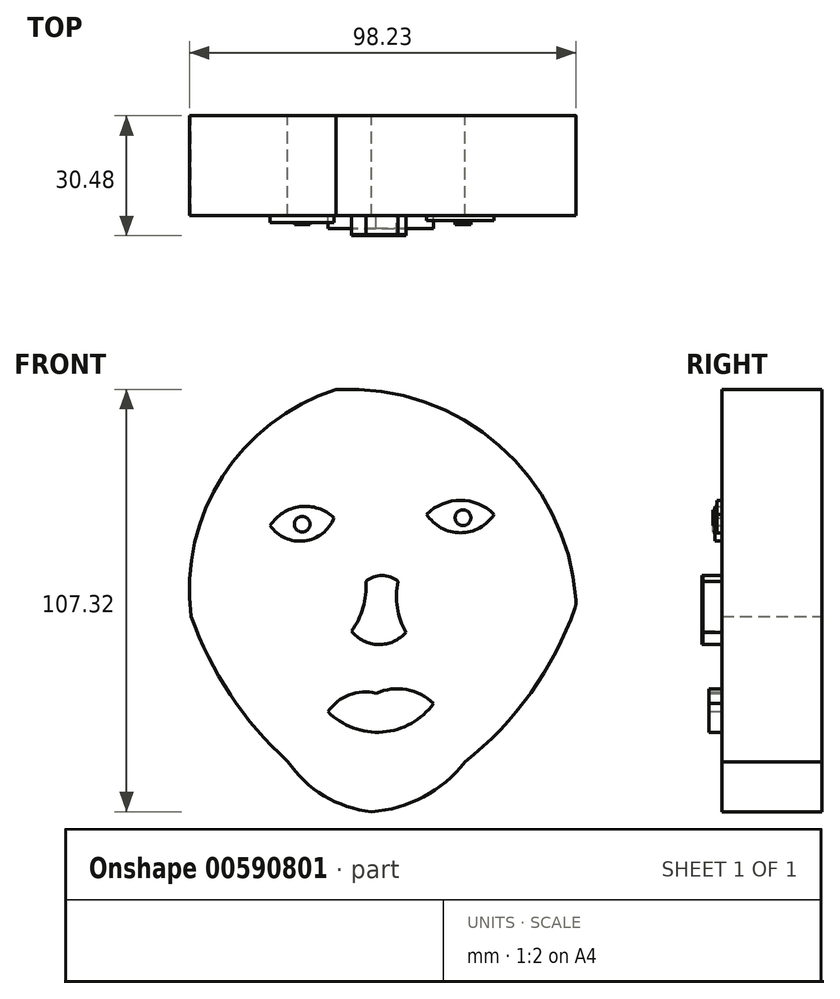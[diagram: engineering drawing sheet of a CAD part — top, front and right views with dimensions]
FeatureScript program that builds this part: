
annotation { "Feature Type Name" : "Feature", "Feature Type Description" : "" }
export const myFeature = defineFeature(function(context is Context, id is Id, definition is map)
    precondition{}
    {
        {
            var Q0;
            Q0=qCreatedBy(makeId("Front.planeOp"),FACE);
            var sketch = newSketch(context, id + "F0", { "sketchPlane" : qUnion([Q0])});
            skArc(sketch, "E0", {"start": v(-3.94, 54.48) * mm, "mid": v(-32.78, 32.37) * mm, "end": v(-40.74, -3.09) * mm});
            skArc(sketch, "E1", {"start": v(57.11, 0) * mm, "mid": v(37.92, 39.94) * mm, "end": v(-3.94, 54.48) * mm});
            skArc(sketch, "E2", {"start": v(-40.74, -3.09) * mm, "mid": v(-30.78, -23.03) * mm, "end": v(-16.23, -39.9) * mm});
            skArc(sketch, "E3", {"start": v(-16.23, -39.9) * mm, "mid": v(-7, -48.7) * mm, "end": v(5.1, -52.74) * mm});
            skArc(sketch, "E4", {"start": v(5.1, -52.74) * mm, "mid": v(18.29, -48.98) * mm, "end": v(28.77, -40.15) * mm});
            skArc(sketch, "E5", {"start": v(28.77, -40.15) * mm, "mid": v(45.86, -22.13) * mm, "end": v(57.11, 0) * mm});
            skSolve(sketch);
        }
        {
            var Q0;
            Q0=makeQuery(id+"F0.imprint","IMPRINT",FACE,{"disambiguationData":[TD([[makeQuery(id+"F0.imprint","IMPRINT",EDGE,{"derivedFrom":sQuery(id+"F0.wireOp",EDGE,"E0")}),1.0]])]});
            extrude(context, id + "F1", {"entities" : qUnion([Q0]), "depth" : 25.4 * mm, "offsetDistance" : 25.4 * mm});
        }
        {
            var Q0;
            Q0=makeQuery(id+"F1.opExtrude","SWEPT_EDGE",EDGE,{"disambiguationData":[OSD([sQuery(id+"F0.wireOp",EDGE,"E1"),sQuery(id+"F0.wireOp",EDGE,"E5")])]});
            fillet(context, id + "F2", {"entities" : qUnion([Q0]), "radius" : 5.08 * mm, "tangentPropagation" : true, "allowEdgeOverflow" : false});
        }
        {
            var Q0;
            Q0=makeQuery(id+"F1.opExtrude","CAP_FACE",FACE,{"disambiguationData":[OSD([sQuery(id+"F0.wireOp",EDGE,"E0"),sQuery(id+"F0.wireOp",EDGE,"E1"),sQuery(id+"F0.wireOp",EDGE,"E2"),sQuery(id+"F0.wireOp",EDGE,"E3"),sQuery(id+"F0.wireOp",EDGE,"E4"),sQuery(id+"F0.wireOp",EDGE,"E5")])],"isStart":false});
            var sketch = newSketch(context, id + "F3", { "sketchPlane" : qUnion([Q0])});
            skArc(sketch, "E6", {"start": v(-11.83, 44.82) * mm, "mid": v(-25.26, 50.26) * mm, "end": v(-38.7, 44.82) * mm});
            skArc(sketch, "E7", {"start": v(-29.05, 57.96) * mm, "mid": v(-21.73, 49.7) * mm, "end": v(-11.83, 44.82) * mm});
            skArc(sketch, "E8", {"start": v(-8.03, 62.64) * mm, "mid": v(-11.09, 53.98) * mm, "end": v(-11.83, 44.82) * mm});
            skArc(sketch, "E9", {"start": v(-18.25, 60) * mm, "mid": v(-14.37, 51.2) * mm, "end": v(-7.15, 44.82) * mm});
            skSolve(sketch);
        }
        {
            var Q0;
            {var subQ9=sQuery(id+"F0.wireOp",EDGE,"E2");var subQ14=makeQuery(id+"F1.opExtrude","CAP_EDGE",EDGE,{"disambiguationData":[OSD([subQ9])],"isStart":false});Q0=makeQuery(id+"F3.imprint","IMPRINT",FACE,{"disambiguationData":[TD([[makeQuery(id+"F3.imprint","IMPRINT",EDGE,{"derivedFrom":subQ14}),1.0]])]});}
            var sketch = newSketch(context, id + "F4", { "sketchPlane" : qUnion([Q0])});
            skArc(sketch, "E10", {"start": v(-9.29, 45.39) * mm, "mid": v(-22.19, 52.37) * mm, "end": v(-36.77, 50.8) * mm});
            skArc(sketch, "E11", {"start": v(2.4, 50.3) * mm, "mid": v(-9.6, 54.9) * mm, "end": v(-22.19, 57.5) * mm});
            skPoint(sketch, "E11.endSnap0", {"position": v(-22.19, 52.37) * mm});
            skArc(sketch, "E12", {"start": v(2.4, 50.3) * mm, "mid": v(-8.36, 51.52) * mm, "end": v(-19.18, 51.58) * mm});
            skArc(sketch, "E13", {"start": v(36.1, 50.3) * mm, "mid": v(22.77, 53.24) * mm, "end": v(9.43, 50.3) * mm});
            skArc(sketch, "E14", {"start": v(36.1, 50.3) * mm, "mid": v(26.93, 50.7) * mm, "end": v(19.45, 45.39) * mm});
            skArc(sketch, "E15", {"start": v(45.24, 45.39) * mm, "mid": v(37.3, 45.56) * mm, "end": v(30.92, 40.8) * mm});
            skArc(sketch, "E16", {"start": v(42.8, 50.3) * mm, "mid": v(33.75, 49.76) * mm, "end": v(25.81, 45.39) * mm});
            skArc(sketch, "E17", {"start": v(42.8, 50.3) * mm, "mid": v(36.17, 49.52) * mm, "end": v(30.92, 45.39) * mm});
            skArc(sketch, "E18", {"start": v(38.66, 53.24) * mm, "mid": v(26.57, 57.77) * mm, "end": v(16.03, 50.3) * mm});
            skPoint(sketch, "E18.startSnap0", {"position": v(22.77, 53.24) * mm});
            skArc(sketch, "E19", {"start": v(58.53, 45.39) * mm, "mid": v(46.41, 44.63) * mm, "end": v(36.1, 38.2) * mm});
            skArc(sketch, "E20", {"start": v(51.08, 53.24) * mm, "mid": v(41.2, 49.1) * mm, "end": v(32.58, 42.76) * mm});
            skArc(sketch, "E21", {"start": v(29.89, 55.18) * mm, "mid": v(19.27, 57.62) * mm, "end": v(9.43, 52.97) * mm});
            skArc(sketch, "E22", {"start": v(2.4, 52.97) * mm, "mid": v(-9.37, 58.06) * mm, "end": v(-22.19, 57.5) * mm});
            skArc(sketch, "E23", {"start": v(-13.81, 42.73) * mm, "mid": v(-24, 47.77) * mm, "end": v(-34.79, 44.23) * mm});
            skArc(sketch, "E24", {"start": v(-14.54, 40.13) * mm, "mid": v(-22.74, 43.62) * mm, "end": v(-31.61, 42.73) * mm});
            skArc(sketch, "E25", {"start": v(-4.54, 46.3) * mm, "mid": v(-12.16, 52.84) * mm, "end": v(-22.19, 52.97) * mm});
            skArc(sketch, "E26", {"start": v(29.89, 55.18) * mm, "mid": v(16.98, 58.22) * mm, "end": v(4.8, 52.97) * mm});
            skArc(sketch, "E27", {"start": v(47.63, 48) * mm, "mid": v(34.16, 46.75) * mm, "end": v(24.61, 37.16) * mm});
            skArc(sketch, "E28", {"start": v(53.1, 40.8) * mm, "mid": v(43.8, 39.51) * mm, "end": v(36.1, 34.08) * mm});
            skArc(sketch, "E29", {"start": v(0, 46.3) * mm, "mid": v(-6.13, 51) * mm, "end": v(-13.81, 50.3) * mm});
            skArc(sketch, "E30", {"start": v(0, 40.8) * mm, "mid": v(-6.55, 48.04) * mm, "end": v(-16.04, 50.3) * mm});
            skArc(sketch, "E31", {"start": v(29.89, 55.18) * mm, "mid": v(18.87, 51.99) * mm, "end": v(9.5, 45.39) * mm});
            skArc(sketch, "E32", {"start": v(36.1, 50.3) * mm, "mid": v(22.97, 51.16) * mm, "end": v(12.86, 42.73) * mm});
            skArc(sketch, "E33", {"start": v(18.84, 40.8) * mm, "mid": v(30.72, 39.65) * mm, "end": v(36.1, 50.3) * mm});
            skArc(sketch, "E34", {"start": v(29.89, 55.18) * mm, "mid": v(16.42, 52.37) * mm, "end": v(5.41, 44.1) * mm});
            skArc(sketch, "E35", {"start": v(6.58, 45.39) * mm, "mid": v(-0.68, 56.95) * mm, "end": v(-13.81, 53.24) * mm});
            skArc(sketch, "E36", {"start": v(-4.54, 41.1) * mm, "mid": v(-22.04, 47.73) * mm, "end": v(-39.41, 40.8) * mm});
            skArc(sketch, "E37", {"start": v(-11.17, 37.6) * mm, "mid": v(-17.96, 47.2) * mm, "end": v(-29.7, 46.5) * mm});
            skArc(sketch, "E38", {"start": v(18.84, 42.73) * mm, "mid": v(29.53, 34.62) * mm, "end": v(37.3, 45.56) * mm});
            skArc(sketch, "E39", {"start": v(-14.93, 33.88) * mm, "mid": v(-19.87, 41.32) * mm, "end": v(-28.51, 39.08) * mm});
            skArc(sketch, "E40", {"start": v(54.54, 36.29) * mm, "mid": v(40.82, 37.8) * mm, "end": v(29.49, 29.9) * mm});
            skSolve(sketch);
        }
        {
            var Q0;
            {var subQ15=sQuery(id+"F0.wireOp",EDGE,"E2");var subQ39=makeQuery(id+"F1.opExtrude","CAP_EDGE",EDGE,{"disambiguationData":[OSD([subQ15])],"isStart":false});var subQ40=makeQuery(id+"F3.imprint","IMPRINT",EDGE,{"derivedFrom":subQ39});Q0=makeQuery(id+"F4.imprint","IMPRINT",FACE,{"disambiguationData":[TD([[makeQuery(id+"F4.imprint","IMPRINT",EDGE,{"derivedFrom":subQ40}),1.0]])]});}
            var sketch = newSketch(context, id + "F5", { "sketchPlane" : qUnion([Q0])});
            skArc(sketch, "E41", {"start": v(-4.45, 21.95) * mm, "mid": v(-13.03, 24.77) * mm, "end": v(-20.66, 19.95) * mm});
            skArc(sketch, "E42", {"start": v(-20.66, 19.95) * mm, "mid": v(-11.95, 16.06) * mm, "end": v(-4.45, 21.95) * mm});
            skSolve(sketch);
        }
        {
            var Q0;
            Q0=makeQuery(id+"F5.imprint","IMPRINT",FACE,{"disambiguationData":[TD([[makeQuery(id+"F5.imprint","IMPRINT",EDGE,{"derivedFrom":sQuery(id+"F5.wireOp",EDGE,"E41")}),-1.0]])]});
            var sketch = newSketch(context, id + "F6", { "sketchPlane" : qUnion([Q0])});
            skArc(sketch, "E43", {"start": v(36.25, 22.84) * mm, "mid": v(27.37, 26.37) * mm, "end": v(18.68, 22.38) * mm});
            skArc(sketch, "E44", {"start": v(19.11, 22.84) * mm, "mid": v(27.68, 18.13) * mm, "end": v(36.25, 22.84) * mm});
            skSolve(sketch);
        }
        {
            var Q0;
            Q0=makeQuery(id+"F5.imprint","IMPRINT",FACE,{"disambiguationData":[TD([[makeQuery(id+"F5.imprint","IMPRINT",EDGE,{"derivedFrom":sQuery(id+"F5.wireOp",EDGE,"E41")}),1.0]])]});
            extrude(context, id + "F7", {"entities" : qUnion([Q0]), "operationType" : NewBodyOperationType.ADD, "depth" : 1.78 * mm, "offsetDistance" : 25.4 * mm});
        }
        {
            var Q0;
            {var subQ0=sQuery(id+"F6.wireOp",EDGE,"E44");Q0=makeQuery(id+"F6.imprint","IMPRINT",FACE,{"disambiguationData":[TD([[makeQuery(id+"F6.imprint","IMPRINT",EDGE,{"derivedFrom":subQ0}),1.0]])]});}
            extrude(context, id + "F8", {"entities" : qUnion([Q0]), "operationType" : NewBodyOperationType.ADD, "depth" : 1.27 * mm, "offsetDistance" : 25.4 * mm});
        }
        {
            var Q0;
            Q0=makeQuery(id+"F7.opExtrude","CAP_FACE",FACE,{"disambiguationData":[OSD([sQuery(id+"F5.wireOp",EDGE,"E41"),sQuery(id+"F5.wireOp",EDGE,"E42")])],"isStart":false});
            var sketch = newSketch(context, id + "F9", { "sketchPlane" : qUnion([Q0])});
            skCircle(sketch, "E45", {"center": v(-12.51, 20.3) * mm, "radius": 1.98 * mm});
            skCircle(sketch, "E46", {"center": v(28.33, 21.95) * mm, "radius": 2 * mm});
            skSolve(sketch);
        }
        {
            var Q0;
            Q0=makeQuery(id+"F9.imprint","IMPRINT",FACE,{"disambiguationData":[TD([[makeQuery(id+"F9.imprint","IMPRINT",EDGE,{"derivedFrom":sQuery(id+"F9.wireOp",EDGE,"E45")}),1.0]])]});
            var Q1;
            Q1=makeQuery(id+"F9.imprint","IMPRINT",FACE,{"disambiguationData":[TD([[makeQuery(id+"F9.imprint","IMPRINT",EDGE,{"derivedFrom":sQuery(id+"F9.wireOp",EDGE,"E46")}),1.0]])]});
            extrude(context, id + "F10", {"entities" : qUnion([Q0, Q1]), "operationType" : NewBodyOperationType.ADD, "depth" : 0.5 * mm, "offsetDistance" : 25.4 * mm});
        }
        {
            var Q0;
            {var subQ9=sQuery(id+"F0.wireOp",EDGE,"E2");var subQ14=makeQuery(id+"F1.opExtrude","CAP_EDGE",EDGE,{"disambiguationData":[OSD([subQ9])],"isStart":false});Q0=makeQuery(id+"F3.imprint","IMPRINT",FACE,{"disambiguationData":[TD([[makeQuery(id+"F3.imprint","IMPRINT",EDGE,{"derivedFrom":subQ14}),1.0]])]});}
            var sketch = newSketch(context, id + "F11", { "sketchPlane" : qUnion([Q0])});
            skArc(sketch, "E47", {"start": v(-6.57, -44.82) * mm, "mid": v(-7.38, -48) * mm, "end": v(-5.11, -50.37) * mm});
            skArc(sketch, "E48", {"start": v(16.8, -46.28) * mm, "mid": v(15.62, -48.32) * mm, "end": v(15.62, -50.66) * mm});
            skArc(sketch, "E49", {"start": v(3.65, -48.32) * mm, "mid": v(2.56, -50.54) * mm, "end": v(2.77, -53) * mm});
            skPoint(sketch, "E49.startSnap0", {"position": v(15.62, -48.32) * mm});
            skArc(sketch, "E50", {"start": v(12.12, -53) * mm, "mid": v(11.87, -50.95) * mm, "end": v(11.53, -48.91) * mm});
            skArc(sketch, "E51", {"start": v(0, -47.14) * mm, "mid": v(-1.42, -50.07) * mm, "end": v(0, -53) * mm});
            skArc(sketch, "E52", {"start": v(7.08, -51.38) * mm, "mid": v(10.4, -52.1) * mm, "end": v(11.53, -48.91) * mm});
            skArc(sketch, "E53", {"start": v(9.14, -49.86) * mm, "mid": v(7.32, -50.9) * mm, "end": v(7.08, -53) * mm});
            skArc(sketch, "E54", {"start": v(11.53, -48.91) * mm, "mid": v(10.87, -53.67) * mm, "end": v(15.62, -53) * mm});
            skArc(sketch, "E55", {"start": v(7.08, -51.38) * mm, "mid": v(9.23, -49.15) * mm, "end": v(6.86, -47.14) * mm});
            skArc(sketch, "E56", {"start": v(0, -44.24) * mm, "mid": v(0.4, -48.93) * mm, "end": v(2.77, -53) * mm});
            skArc(sketch, "E57", {"start": v(15.62, -50.66) * mm, "mid": v(20.3, -49.13) * mm, "end": v(19.71, -44.24) * mm});
            skSolve(sketch);
        }
        {
            var Q0;
            {var subQ9=sQuery(id+"F0.wireOp",EDGE,"E2");var subQ14=makeQuery(id+"F1.opExtrude","CAP_EDGE",EDGE,{"disambiguationData":[OSD([subQ9])],"isStart":false});Q0=makeQuery(id+"F3.imprint","IMPRINT",FACE,{"disambiguationData":[TD([[makeQuery(id+"F3.imprint","IMPRINT",EDGE,{"derivedFrom":subQ14}),1.0]])]});}
            var sketch = newSketch(context, id + "F12", { "sketchPlane" : qUnion([Q0])});
            skArc(sketch, "E58", {"start": v(6.28, -22.63) * mm, "mid": v(-0.56, -23.1) * mm, "end": v(-5.99, -27.3) * mm});
            skArc(sketch, "E59", {"start": v(20.88, -25.26) * mm, "mid": v(13.98, -21.73) * mm, "end": v(6.28, -22.63) * mm});
            skArc(sketch, "E60", {"start": v(-5.99, -27.3) * mm, "mid": v(7.92, -32.5) * mm, "end": v(20.88, -25.26) * mm});
            skSolve(sketch);
        }
        {
            var Q0;
            Q0 = qSketchRegion(id + "F12", true);
            extrude(context, id + "F13", {"entities" : qUnion([Q0]), "operationType" : NewBodyOperationType.ADD, "depth" : 3.3 * mm, "offsetDistance" : 25.4 * mm});
        }
        {
            var Q0;
            {var subQ10=sQuery(id+"F0.wireOp",EDGE,"E2");var subQ11=makeQuery(id+"F1.opExtrude","CAP_EDGE",EDGE,{"disambiguationData":[OSD([subQ10])],"isStart":false});var subQ20=makeQuery(id+"F3.imprint","IMPRINT",EDGE,{"derivedFrom":subQ11});Q0=makeQuery(id+"F11.imprint","IMPRINT",FACE,{"disambiguationData":[TD([[makeQuery(id+"F11.imprint","IMPRINT",EDGE,{"derivedFrom":subQ20}),1.0]])]});}
            var sketch = newSketch(context, id + "F14", { "sketchPlane" : qUnion([Q0])});
            skArc(sketch, "E61", {"start": v(0, -6.86) * mm, "mid": v(2.93, -0.9) * mm, "end": v(3.65, 5.7) * mm});
            skArc(sketch, "E62", {"start": v(11.83, 5.7) * mm, "mid": v(11.64, -0.92) * mm, "end": v(13.87, -7.15) * mm});
            skArc(sketch, "E63", {"start": v(0, -6.86) * mm, "mid": v(6.87, -10.27) * mm, "end": v(13.87, -7.15) * mm});
            skArc(sketch, "E64", {"start": v(11.83, 5.7) * mm, "mid": v(7.74, 7.31) * mm, "end": v(3.65, 5.7) * mm});
            skSolve(sketch);
        }
        {
            var Q0;
            Q0 = qSketchRegion(id + "F14", true);
            extrude(context, id + "F15", {"entities" : qUnion([Q0]), "depth" : 4.83 * mm, "offsetDistance" : 25.4 * mm});
        }
        {
            var Q0;
            Q0 = qSketchRegion(id + "F14", true);
            extrude(context, id + "F16", {"entities" : qUnion([Q0]), "depth" : 5.08 * mm, "offsetDistance" : 25.4 * mm});
        }
    });
